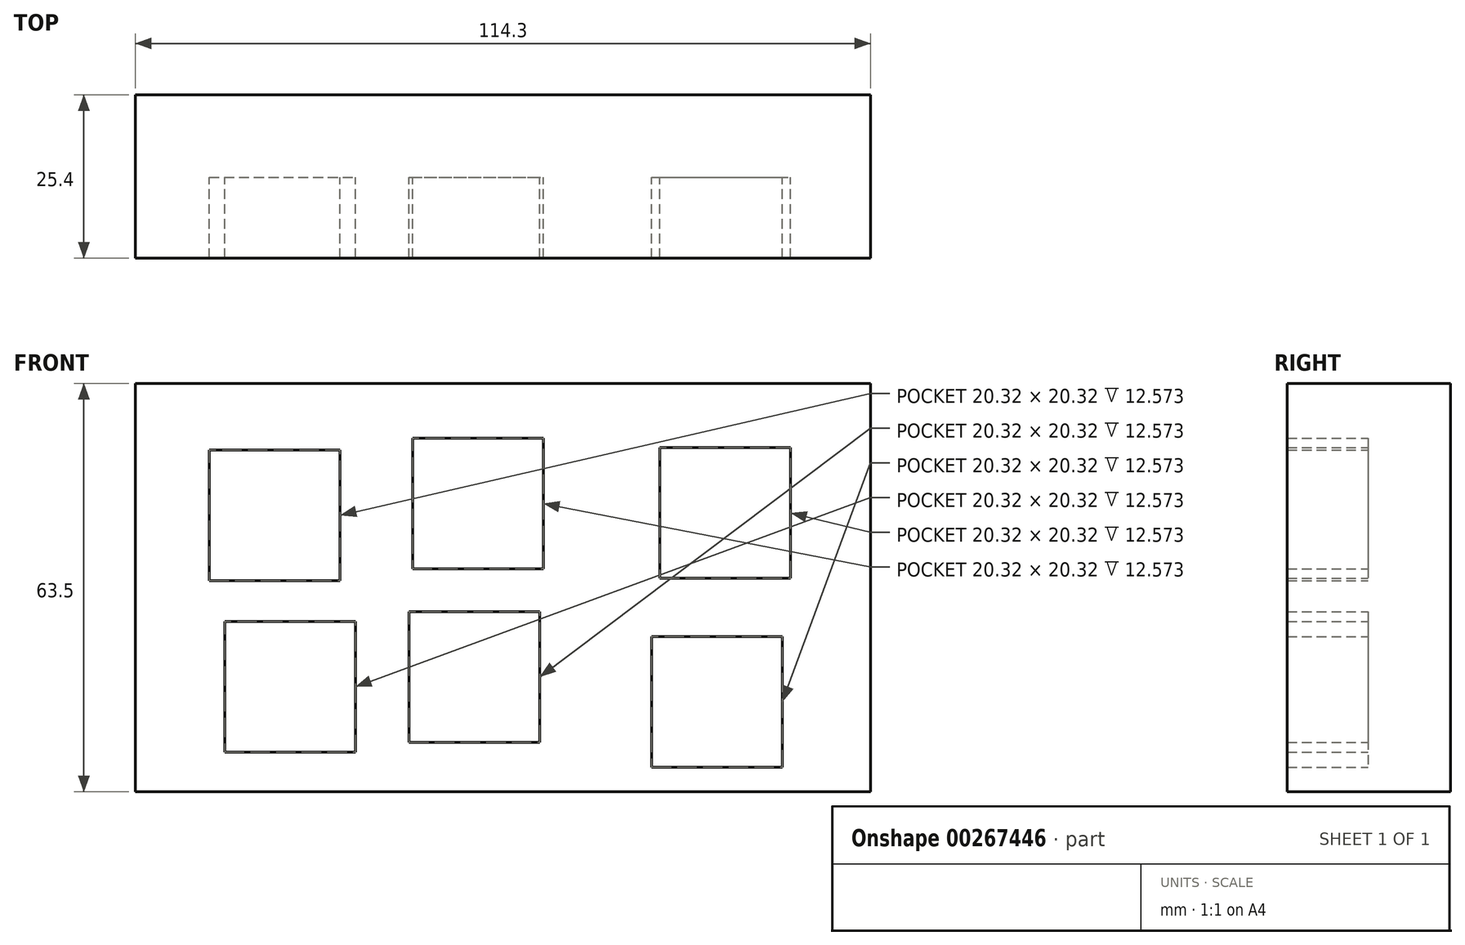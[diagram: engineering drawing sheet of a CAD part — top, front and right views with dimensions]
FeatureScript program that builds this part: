
annotation { "Feature Type Name" : "Feature", "Feature Type Description" : "" }
export const myFeature = defineFeature(function(context is Context, id is Id, definition is map)
    precondition{}
    {
        {
            var Q0;
            Q0=qCreatedBy(makeId("Front.planeOp"),FACE);
            var sketch = newSketch(context, id + "F0", { "sketchPlane" : qUnion([Q0])});
            skLineSegment(sketch, "E0.bottom", {"start": v(57.15, -31.75) * mm, "end": v(-57.15, -31.75) * mm});
            skLineSegment(sketch, "E0.top", {"start": v(57.15, 31.75) * mm, "end": v(-57.15, 31.75) * mm});
            skLineSegment(sketch, "E0.left", {"start": v(57.15, -31.75) * mm, "end": v(57.15, 31.75) * mm});
            skLineSegment(sketch, "E0.right", {"start": v(-57.15, -31.75) * mm, "end": v(-57.15, 31.75) * mm});
            skPoint(sketch, "E0.middle", {"position": v(0, 0) * mm});
            skSolve(sketch);
        }
        {
            var Q0;
            Q0=makeQuery(id+"F0.imprint","IMPRINT",FACE,{"disambiguationData":[TD([[makeQuery(id+"F0.imprint","IMPRINT",EDGE,{"derivedFrom":sQuery(id+"F0.wireOp",EDGE,"E0.bottom")}),-1.0]])]});
            extrude(context, id + "F1", {"entities" : qUnion([Q0]), "depth" : 25.4 * mm});
        }
        {
            var Q0;
            Q0=makeQuery(id+"F1.opExtrude","CAP_FACE",FACE,{"disambiguationData":[OSD([sQuery(id+"F0.wireOp",EDGE,"E0.bottom"),sQuery(id+"F0.wireOp",EDGE,"E0.top"),sQuery(id+"F0.wireOp",EDGE,"E0.left"),sQuery(id+"F0.wireOp",EDGE,"E0.right")])],"isStart":false});
            var sketch = newSketch(context, id + "F2", { "sketchPlane" : qUnion([Q0])});
            skLineSegment(sketch, "E1.bottom", {"start": v(-45.63, 21.43) * mm, "end": v(-25.31, 21.43) * mm});
            skLineSegment(sketch, "E1.top", {"start": v(-45.63, 1.1) * mm, "end": v(-25.31, 1.1) * mm});
            skLineSegment(sketch, "E1.left", {"start": v(-45.63, 21.43) * mm, "end": v(-45.63, 1.1) * mm});
            skLineSegment(sketch, "E1.right", {"start": v(-25.31, 21.43) * mm, "end": v(-25.31, 1.1) * mm});
            skLineSegment(sketch, "E2.bottom", {"start": v(-14.06, 23.24) * mm, "end": v(6.26, 23.24) * mm});
            skLineSegment(sketch, "E2.top", {"start": v(-14.06, 2.92) * mm, "end": v(6.26, 2.92) * mm});
            skLineSegment(sketch, "E2.left", {"start": v(-14.06, 23.24) * mm, "end": v(-14.06, 2.92) * mm});
            skLineSegment(sketch, "E2.right", {"start": v(6.26, 23.24) * mm, "end": v(6.26, 2.92) * mm});
            skLineSegment(sketch, "E3.bottom", {"start": v(24.4, 21.8) * mm, "end": v(44.72, 21.8) * mm});
            skLineSegment(sketch, "E3.top", {"start": v(24.4, 1.47) * mm, "end": v(44.72, 1.47) * mm});
            skLineSegment(sketch, "E3.left", {"start": v(24.4, 21.8) * mm, "end": v(24.4, 1.47) * mm});
            skLineSegment(sketch, "E3.right", {"start": v(44.72, 21.8) * mm, "end": v(44.72, 1.47) * mm});
            skLineSegment(sketch, "E4.bottom", {"start": v(-43.27, -5.24) * mm, "end": v(-22.95, -5.24) * mm});
            skLineSegment(sketch, "E4.top", {"start": v(-43.27, -25.56) * mm, "end": v(-22.95, -25.56) * mm});
            skLineSegment(sketch, "E4.left", {"start": v(-43.27, -5.24) * mm, "end": v(-43.27, -25.56) * mm});
            skLineSegment(sketch, "E4.right", {"start": v(-22.95, -5.24) * mm, "end": v(-22.95, -25.56) * mm});
            skLineSegment(sketch, "E5.bottom", {"start": v(23.13, -7.6) * mm, "end": v(43.45, -7.6) * mm});
            skLineSegment(sketch, "E5.top", {"start": v(23.13, -27.92) * mm, "end": v(43.45, -27.92) * mm});
            skLineSegment(sketch, "E5.left", {"start": v(23.13, -7.6) * mm, "end": v(23.13, -27.92) * mm});
            skLineSegment(sketch, "E5.right", {"start": v(43.45, -7.6) * mm, "end": v(43.45, -27.92) * mm});
            skLineSegment(sketch, "E6.bottom", {"start": v(-14.58, -3.72) * mm, "end": v(5.74, -3.72) * mm});
            skLineSegment(sketch, "E6.top", {"start": v(-14.58, -24.04) * mm, "end": v(5.74, -24.04) * mm});
            skLineSegment(sketch, "E6.left", {"start": v(-14.58, -3.72) * mm, "end": v(-14.58, -24.04) * mm});
            skLineSegment(sketch, "E6.right", {"start": v(5.74, -3.72) * mm, "end": v(5.74, -24.04) * mm});
            skSolve(sketch);
        }
        {
            var Q0;
            Q0 = qSketchRegion(id + "F2", true);
            var Q1;
            Q1=sQuery(id+"F2.wireOp",EDGE,"E1.left");
            var Q2;
            Q2=sQuery(id+"F2.wireOp",EDGE,"E1.bottom");
            var Q3;
            Q3=sQuery(id+"F2.wireOp",EDGE,"E1.right");
            var Q4;
            Q4=sQuery(id+"F2.wireOp",EDGE,"E1.top");
            var Q5;
            Q5=sQuery(id+"F2.wireOp",EDGE,"E2.left");
            var Q6;
            Q6=sQuery(id+"F2.wireOp",EDGE,"E2.top");
            var Q7;
            Q7=sQuery(id+"F2.wireOp",EDGE,"E2.right");
            var Q8;
            Q8=sQuery(id+"F2.wireOp",EDGE,"E2.bottom");
            var Q9;
            Q9=sQuery(id+"F2.wireOp",EDGE,"E3.left");
            var Q10;
            Q10=sQuery(id+"F2.wireOp",EDGE,"E3.top");
            var Q11;
            Q11=sQuery(id+"F2.wireOp",EDGE,"E3.right");
            var Q12;
            Q12=sQuery(id+"F2.wireOp",EDGE,"E3.bottom");
            var Q13;
            Q13=sQuery(id+"F2.wireOp",EDGE,"E5.bottom");
            var Q14;
            Q14=sQuery(id+"F2.wireOp",EDGE,"E5.right");
            var Q15;
            Q15=sQuery(id+"F2.wireOp",EDGE,"E5.left");
            var Q16;
            Q16=sQuery(id+"F2.wireOp",EDGE,"E5.top");
            var Q17;
            Q17=sQuery(id+"F2.wireOp",EDGE,"E6.right");
            var Q18;
            Q18=sQuery(id+"F2.wireOp",EDGE,"E6.bottom");
            var Q19;
            Q19=sQuery(id+"F2.wireOp",EDGE,"E6.left");
            var Q20;
            Q20=sQuery(id+"F2.wireOp",EDGE,"E6.top");
            var Q21;
            Q21=sQuery(id+"F2.wireOp",EDGE,"E4.right");
            var Q22;
            Q22=sQuery(id+"F2.wireOp",EDGE,"E4.bottom");
            var Q23;
            Q23=sQuery(id+"F2.wireOp",EDGE,"E4.left");
            var Q24;
            Q24=sQuery(id+"F2.wireOp",EDGE,"E4.top");
            extrude(context, id + "F3", {"entities" : qUnion([Q0]), "operationType" : NewBodyOperationType.REMOVE, "surfaceEntities" : qUnion([Q1, Q2, Q3, Q4, Q5, Q6, Q7, Q8, Q9, Q10, Q11, Q12, Q13, Q14, Q15, Q16, Q17, Q18, Q19, Q20, Q21, Q22, Q23, Q24]), "endBound" : BoundingType.SYMMETRIC, "depth" : 25.15 * mm});
        }
    });
